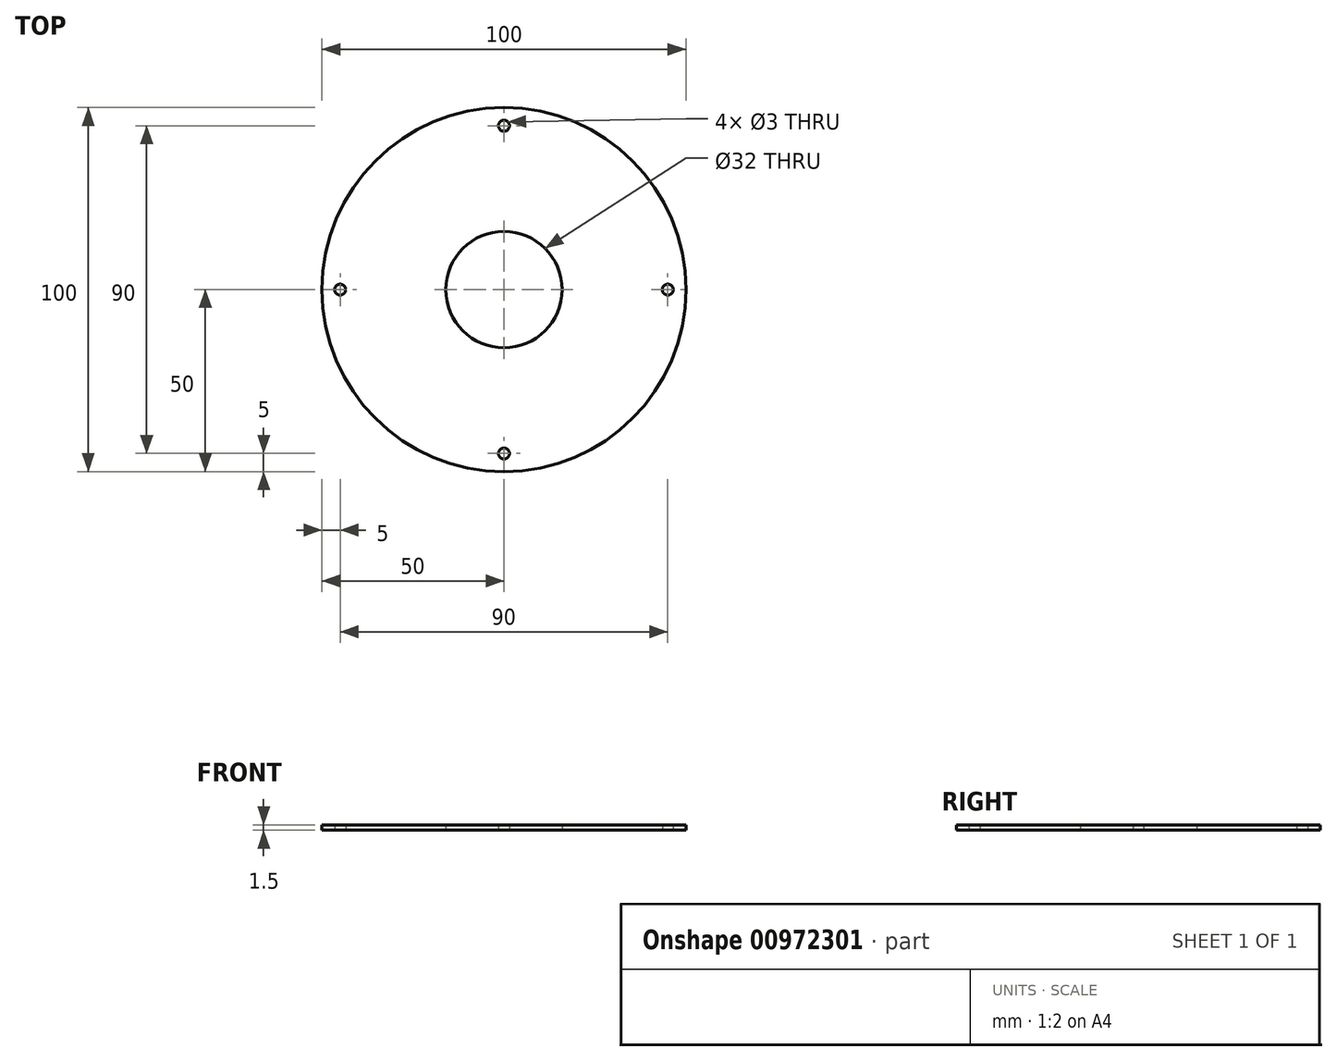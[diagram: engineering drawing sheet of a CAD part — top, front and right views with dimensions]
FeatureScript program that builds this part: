
annotation { "Feature Type Name" : "Feature", "Feature Type Description" : "" }
export const myFeature = defineFeature(function(context is Context, id is Id, definition is map)
    precondition{}
    {
        {
            var Q0;
            Q0=qCreatedBy(makeId("Top.planeOp"),FACE);
            var sketch = newSketch(context, id + "F0", { "sketchPlane" : qUnion([Q0])});
            skCircle(sketch, "E0", {"center": v(0, 0) * mm, "radius": 16 * mm});
            skCircle(sketch, "E1", {"center": v(0, 0) * mm, "radius": 50 * mm});
            skCircle(sketch, "E2", {"center": v(0, 45) * mm, "radius": 1.5 * mm});
            skCircle(sketch, "E3.1.0", {"center": v(-45, 0) * mm, "radius": 1.5 * mm});
            skCircle(sketch, "E3.2.0", {"center": v(0, -45) * mm, "radius": 1.5 * mm});
            skCircle(sketch, "E3.3.0", {"center": v(45, 0) * mm, "radius": 1.5 * mm});
            skSolve(sketch);
        }
        {
            var Q0;
            Q0=makeQuery(id+"F0.imprint","IMPRINT",FACE,{"disambiguationData":[TD([[makeQuery(id+"F0.imprint","IMPRINT",EDGE,{"derivedFrom":sQuery(id+"F0.wireOp",EDGE,"E0")}),-1.0]])]});
            extrude(context, id + "F1", {"entities" : qUnion([Q0]), "depth" : 1.5 * mm, "offsetDistance" : 25 * mm});
        }
    });
